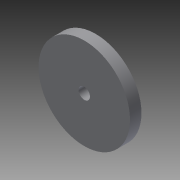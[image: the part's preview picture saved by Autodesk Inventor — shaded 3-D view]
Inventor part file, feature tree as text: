
AUTODESK INVENTOR PART (.ipt)
format: ipt  version: 2013 (Build 170138000, 138)  size: 79,872 bytes
history: native  units: in
note: dims shown in document units (in); Inventor stores cm internally (conversion verified against a paired STEP export)
features: extrude x2, sketch x2
ambient origin geometry x8: Origin, YZ Plane, XZ Plane, XY Plane, X Axis, Y Axis, Z Axis, Center Point
bodies: Solid1 (feature_tree)
feature tree (4):
  extrude  "Extrusion1"  Depth=0.375in TaperAngle=0.0deg
  extrude  "Extrusion2"  Depth=0.375in TaperAngle=0.0deg
  sketch  "Sketch1"  dims[d0=3.0in d1=0.375in d2=0.0in]
  sketch  "Sketch2"  dims[d3=0.375in d4=0.375in d5=0.0in]
